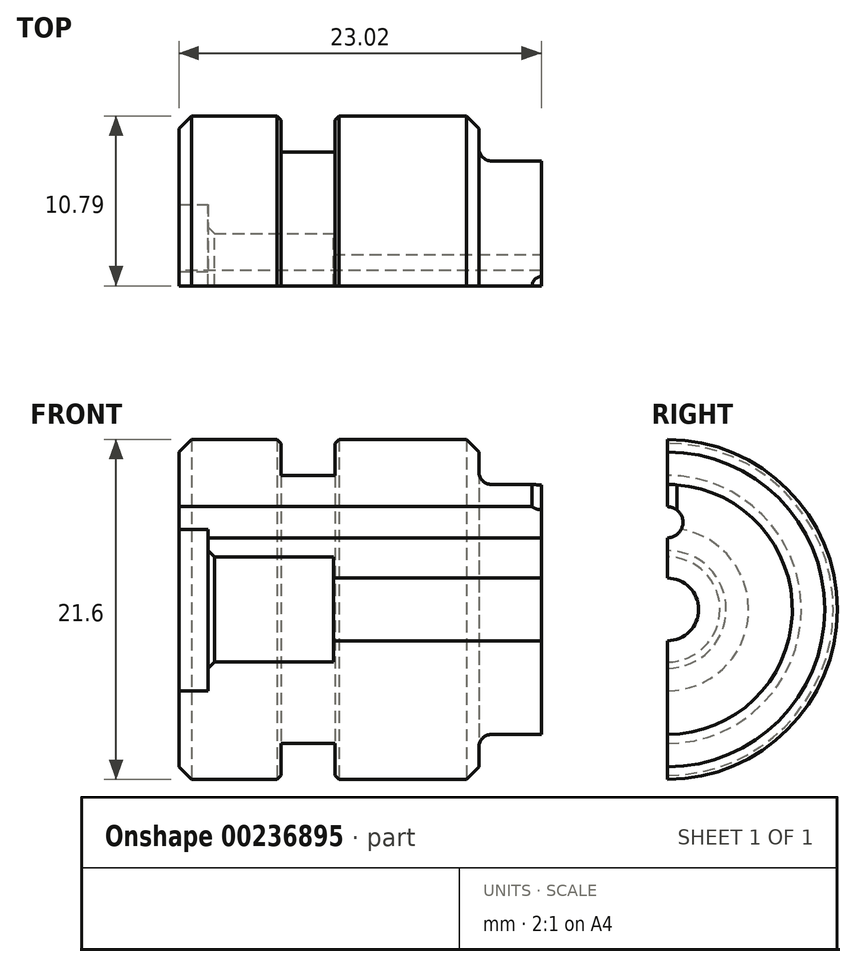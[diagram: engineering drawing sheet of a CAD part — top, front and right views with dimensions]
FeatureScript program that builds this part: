
annotation { "Feature Type Name" : "Feature", "Feature Type Description" : "" }
export const myFeature = defineFeature(function(context is Context, id is Id, definition is map)
    precondition{}
    {
        {
            var Q0;
            Q0=qCreatedBy(makeId("Front.planeOp"),FACE);
            var sketch = newSketch(context, id + "F0", { "sketchPlane" : qUnion([Q0])});
            skLineSegment(sketch, "E0.bottom", {"start": v(-29.86, 10.8) * mm, "end": v(-24.42, 10.8) * mm});
            skLineSegment(sketch, "E0.top", {"start": v(-30.66, 0) * mm, "end": v(0, 0) * mm});
            skLineSegment(sketch, "E0.left", {"start": v(-30.66, 10) * mm, "end": v(-30.66, 0) * mm});
            skLineSegment(sketch, "E0.right", {"start": v(0, 5.87) * mm, "end": v(0, 0) * mm});
            skLineSegment(sketch, "E1", {"start": v(-3.97, 7.94) * mm, "end": v(-10.81, 7.94) * mm});
            skLineSegment(sketch, "E2", {"start": v(-11.6, 8.73) * mm, "end": v(-11.6, 10) * mm});
            skLineSegment(sketch, "E3", {"start": v(-3.97, 7.94) * mm, "end": v(-1.57, 6.7) * mm});
            skPoint(sketch, "E4", {"position": v(-1.57, 6.7) * mm});
            skLineSegment(sketch, "E5", {"start": v(-1.57, 6.7) * mm, "end": v(0, 5.87) * mm});
            skPoint(sketch, "E6.visualSharp", {"position": v(-11.6, 7.94) * mm});
            skArc(sketch, "E6.filletArc", {"start": v(-11.6, 8.73) * mm, "mid": v(-11.38, 8.17) * mm, "end": v(-10.81, 7.94) * mm});
            skLineSegment(sketch, "E7", {"start": v(-12.4, 10.8) * mm, "end": v(-11.6, 10) * mm});
            skLineSegment(sketch, "E8", {"start": v(-30.66, 10) * mm, "end": v(-29.86, 10.8) * mm});
            skLineSegment(sketch, "E9.top", {"start": v(-24.16, 8.5) * mm, "end": v(-20.74, 8.5) * mm});
            skLineSegment(sketch, "E9.left", {"start": v(-24.16, 10.54) * mm, "end": v(-24.16, 8.5) * mm});
            skLineSegment(sketch, "E9.right", {"start": v(-20.74, 10.54) * mm, "end": v(-20.74, 8.5) * mm});
            skLineSegment(sketch, "E10.trimOffspring", {"start": v(-20.48, 10.8) * mm, "end": v(-12.4, 10.8) * mm});
            skLineSegment(sketch, "E11", {"start": v(-24.42, 10.8) * mm, "end": v(-24.16, 10.54) * mm});
            skLineSegment(sketch, "E12", {"start": v(-20.74, 10.54) * mm, "end": v(-20.48, 10.8) * mm});
            skSolve(sketch);
        }
        {
            var Q0;
            Q0=makeQuery(id+"F0.imprint","IMPRINT",FACE,{"disambiguationData":[TD([[makeQuery(id+"F0.imprint","IMPRINT",EDGE,{"derivedFrom":sQuery(id+"F0.wireOp",EDGE,"E0.bottom")}),-1.0]])]});
            var Q1;
            Q1=sQuery(id+"F0.wireOp",EDGE,"E0.top");
            revolve(context, id + "F1", {"entities" : qUnion([Q0]), "axis" : qUnion([Q1]), "revolveType" : RevolveType.FULL});
        }
        {
            var Q0;
            Q0=makeQuery(id+"F1.opRevolve","SWEPT_FACE",FACE,{"disambiguationData":[OSD([sQuery(id+"F0.wireOp",EDGE,"E0.right")])]});
            var sketch = newSketch(context, id + "F2", { "sketchPlane" : qUnion([Q0])});
            skCircle(sketch, "E13", {"center": v(0, 0) * mm, "radius": 1.98 * mm});
            skSolve(sketch);
        }
        {
            var Q0;
            Q0 = qSketchRegion(id + "F2", true);
            extrude(context, id + "F3", {"entities" : qUnion([Q0]), "operationType" : NewBodyOperationType.REMOVE, "endBound" : BoundingType.THROUGH_ALL, "oppositeDirection" : true, "depth" : 25.4 * mm});
        }
        {
            var Q0;
            Q0=qCreatedBy(makeId("Front.planeOp"),FACE);
            var sketch = newSketch(context, id + "F4", { "sketchPlane" : qUnion([Q0])});
            skLineSegment(sketch, "E14.bottom", {"start": v(-30.66, 0) * mm, "end": v(-28.8, 0) * mm});
            skLineSegment(sketch, "E14.top", {"start": v(-30.66, 5.16) * mm, "end": v(-28.8, 5.16) * mm});
            skLineSegment(sketch, "E14.left", {"start": v(-30.66, 0) * mm, "end": v(-30.66, 5.16) * mm});
            skLineSegment(sketch, "E14.right", {"start": v(-28.8, 3.74) * mm, "end": v(-28.8, 5.16) * mm});
            skLineSegment(sketch, "E15.bottom", {"start": v(-28.4, 3.34) * mm, "end": v(-20.85, 3.34) * mm});
            skLineSegment(sketch, "E15.top", {"start": v(-28.8, 0) * mm, "end": v(-20.85, 0) * mm});
            skLineSegment(sketch, "E15.right", {"start": v(-20.85, 3.34) * mm, "end": v(-20.85, 0) * mm});
            skLineSegment(sketch, "E16", {"start": v(-28.8, 3.74) * mm, "end": v(-28.4, 3.34) * mm});
            skSolve(sketch);
        }
        {
            var Q0;
            Q0 = qSketchRegion(id + "F4", true);
            var Q1;
            Q1=sQuery(id+"F4.wireOp",EDGE,"E15.top");
            revolve(context, id + "F5", {"operationType" : NewBodyOperationType.REMOVE, "entities" : qUnion([Q0]), "axis" : qUnion([Q1]), "revolveType" : RevolveType.FULL, "oppositeDirection" : true});
        }
        {
            var Q0;
            Q0=qCreatedBy(makeId("Front.planeOp"),FACE);
            var sketch = newSketch(context, id + "F6", { "sketchPlane" : qUnion([Q0])});
            skLineSegment(sketch, "E17.bottom", {"start": v(-30.66, 6.55) * mm, "end": v(-5.26, 6.55) * mm});
            skLineSegment(sketch, "E17.top", {"start": v(-30.66, 5.56) * mm, "end": v(-22.47, 5.56) * mm});
            skLineSegment(sketch, "E17.left", {"start": v(-30.66, 6.55) * mm, "end": v(-30.66, 5.56) * mm});
            skLineSegment(sketch, "E18", {"start": v(-5.26, 6.55) * mm, "end": v(-4.66, 5.56) * mm});
            skLineSegment(sketch, "E19", {"start": v(-4.66, 5.56) * mm, "end": v(-22.47, 5.56) * mm});
            skSolve(sketch);
        }
        {
            var Q0;
            Q0=qCreatedBy(makeId("Front.planeOp"),FACE);
            var sketch = newSketch(context, id + "F7", { "sketchPlane" : qUnion([Q0])});
            skLineSegment(sketch, "E20.bottom", {"start": v(-8.23, 5.56) * mm, "end": v(-7.64, 5.56) * mm});
            skLineSegment(sketch, "E20.top", {"start": v(-8.23, 10.2) * mm, "end": v(-7.64, 10.2) * mm});
            skLineSegment(sketch, "E20.left", {"start": v(-8.23, 10.2) * mm, "end": v(-8.23, 5.56) * mm});
            skPoint(sketch, "E21", {"position": v(-7.64, 5.56) * mm});
            skLineSegment(sketch, "E22", {"start": v(-7.64, 10.2) * mm, "end": v(-7.64, 5.56) * mm});
            skSolve(sketch);
        }
        {
            var Q0;
            Q0 = qSketchRegion(id + "F7", true);
            var Q1;
            Q1=sQuery(id+"F7.wireOp",EDGE,"E22");
            revolve(context, id + "F8", {"operationType" : NewBodyOperationType.REMOVE, "entities" : qUnion([Q0]), "axis" : qUnion([Q1]), "revolveType" : RevolveType.FULL, "oppositeDirection" : true});
        }
        {
            var Q0;
            Q0=makeQuery(id+"F1.opRevolve","SWEPT_FACE",FACE,{"disambiguationData":[OSD([sQuery(id+"F0.wireOp",EDGE,"E0.left")])]});
            var sketch = newSketch(context, id + "F9", { "sketchPlane" : qUnion([Q0])});
            skLineSegment(sketch, "E23", {"start": v(0, 0) * mm, "end": v(0, 14.89) * mm});
            skLineSegment(sketch, "E24", {"start": v(0, 14.89) * mm, "end": v(12.7, 14.89) * mm});
            skLineSegment(sketch, "E25", {"start": v(12.7, 14.89) * mm, "end": v(12.7, -15.47) * mm});
            skLineSegment(sketch, "E26", {"start": v(12.7, -15.47) * mm, "end": v(0, -15.47) * mm});
            skLineSegment(sketch, "E27", {"start": v(0, -15.47) * mm, "end": v(0, 0) * mm});
            skSolve(sketch);
        }
        {
            var Q0;
            Q0=makeQuery(id+"F1.opRevolve","SWEPT_FACE",FACE,{"disambiguationData":[OSD([sQuery(id+"F0.wireOp",EDGE,"E0.left")])]});
            var sketch = newSketch(context, id + "F10", { "sketchPlane" : qUnion([Q0])});
            skCircle(sketch, "E28", {"center": v(0, 5.54) * mm, "radius": 1 * mm});
            skLineSegment(sketch, "E29", {"start": v(0, 5.54) * mm, "end": v(0, 0) * mm, "construction": true});
            skSolve(sketch);
        }
        {
            var Q0;
            {var subQ0=sQuery(id+"F10.wireOp",EDGE,"E28");var subQ1=makeQuery(id+"F5.boolean.opBoolean","COPY",EDGE,{"derivedFrom":makeQuery(id+"F5.opRevolve","SWEPT_EDGE",EDGE,{"disambiguationData":[OSD([sQuery(id+"F4.wireOp",EDGE,"E14.top"),sQuery(id+"F4.wireOp",EDGE,"E14.left")])]})});var subQ2=makeQuery(id+"F10.imprint","INTERSECT",VERTEX,{"disambiguationData":[OD(0.0)],"derivedFrom":[subQ1,subQ0]});Q0=makeQuery(id+"F10.imprint","IMPRINT",FACE,{"disambiguationData":[TD([[makeQuery(id+"F10.imprint","IMPRINT",EDGE,{"disambiguationData":[TD([[subQ2,1.0]])],"derivedFrom":subQ0}),1.0]])]});}
            var Q1;
            {var subQ0=sQuery(id+"F10.wireOp",EDGE,"E28");var subQ1=makeQuery(id+"F5.boolean.opBoolean","COPY",EDGE,{"derivedFrom":makeQuery(id+"F5.opRevolve","SWEPT_EDGE",EDGE,{"disambiguationData":[OSD([sQuery(id+"F4.wireOp",EDGE,"E14.top"),sQuery(id+"F4.wireOp",EDGE,"E14.left")])]})});var subQ2=makeQuery(id+"F10.imprint","INTERSECT",VERTEX,{"disambiguationData":[OD(0.0)],"derivedFrom":[subQ1,subQ0]});Q1=makeQuery(id+"F10.imprint","IMPRINT",FACE,{"disambiguationData":[TD([[makeQuery(id+"F10.imprint","IMPRINT",EDGE,{"disambiguationData":[TD([[subQ2,-1.0]])],"derivedFrom":subQ0}),1.0]])]});}
            extrude(context, id + "F11", {"entities" : qUnion([Q0, Q1]), "operationType" : NewBodyOperationType.REMOVE, "oppositeDirection" : true, "depth" : 25.4 * mm});
        }
        {
            var Q0;
            Q0 = qSketchRegion(id + "F9", true);
            extrude(context, id + "F12", {"entities" : qUnion([Q0]), "operationType" : NewBodyOperationType.REMOVE, "endBound" : BoundingType.THROUGH_ALL, "oppositeDirection" : true, "depth" : 25.4 * mm});
        }
        {
            var Q0;
            Q0=makeQuery(id+"F1.opRevolve","SWEPT_EDGE",EDGE,{"disambiguationData":[OSD([sQuery(id+"F0.wireOp",EDGE,"E0.right"),sQuery(id+"F0.wireOp",EDGE,"E5")])]});
            fillet(context, id + "F13", {"entities" : qUnion([Q0]), "radius" : 0.25 * mm, "tangentPropagation" : true, "allowEdgeOverflow" : false});
        }
        {
            var Q0;
            Q0=makeQuery(id+"F12.boolean.opBoolean","COPY",FACE,{"disambiguationData":[TD([makeQuery(id+"F1.opRevolve","SWEPT_FACE",FACE,{"disambiguationData":[OSD([sQuery(id+"F0.wireOp",EDGE,"E0.bottom")])]}),makeQuery(id+"F1.opRevolve","SWEPT_FACE",FACE,{"disambiguationData":[OSD([sQuery(id+"F0.wireOp",EDGE,"E0.left")])]}),makeQuery(id+"F1.opRevolve","SWEPT_FACE",FACE,{"disambiguationData":[OSD([sQuery(id+"F0.wireOp",EDGE,"E1")])]}),makeQuery(id+"F1.opRevolve","SWEPT_FACE",FACE,{"disambiguationData":[OSD([sQuery(id+"F0.wireOp",EDGE,"E2")])]}),makeQuery(id+"F1.opRevolve","SWEPT_FACE",FACE,{"disambiguationData":[OSD([sQuery(id+"F0.wireOp",EDGE,"E6.filletArc")])]}),makeQuery(id+"F1.opRevolve","SWEPT_FACE",FACE,{"disambiguationData":[OSD([sQuery(id+"F0.wireOp",EDGE,"E7")])]}),makeQuery(id+"F1.opRevolve","SWEPT_FACE",FACE,{"disambiguationData":[OSD([sQuery(id+"F0.wireOp",EDGE,"E8")])]}),makeQuery(id+"F1.opRevolve","SWEPT_FACE",FACE,{"disambiguationData":[OSD([sQuery(id+"F0.wireOp",EDGE,"E9.top")])]}),makeQuery(id+"F1.opRevolve","SWEPT_FACE",FACE,{"disambiguationData":[OSD([sQuery(id+"F0.wireOp",EDGE,"E9.left")])]}),makeQuery(id+"F1.opRevolve","SWEPT_FACE",FACE,{"disambiguationData":[OSD([sQuery(id+"F0.wireOp",EDGE,"E9.right")])]}),makeQuery(id+"F1.opRevolve","SWEPT_FACE",FACE,{"disambiguationData":[OSD([sQuery(id+"F0.wireOp",EDGE,"E10.trimOffspring")])]}),makeQuery(id+"F1.opRevolve","SWEPT_FACE",FACE,{"disambiguationData":[OSD([sQuery(id+"F0.wireOp",EDGE,"E11")])]}),makeQuery(id+"F1.opRevolve","SWEPT_FACE",FACE,{"disambiguationData":[OSD([sQuery(id+"F0.wireOp",EDGE,"E12")])]}),makeQuery(id+"F8.boolean.opBoolean","COPY",FACE,{"derivedFrom":makeQuery(id+"F8.opRevolve","SWEPT_FACE",FACE,{"disambiguationData":[OSD([sQuery(id+"F7.wireOp",EDGE,"E20.left")])]})}),makeQuery(id+"F11.boolean.opBoolean","COPY",FACE,{"derivedFrom":makeQuery(id+"F11.opExtrude","SWEPT_FACE",FACE,{"disambiguationData":[OSD([sQuery(id+"F10.wireOp",EDGE,"E28")])]})})])],"derivedFrom":makeQuery(id+"F12.opExtrude","SWEPT_FACE",FACE,{"disambiguationData":[OSD([sQuery(id+"F9.wireOp",EDGE,"E23"),sQuery(id+"F9.wireOp",EDGE,"E27")])]})});
            var sketch = newSketch(context, id + "F14", { "sketchPlane" : qUnion([Q0])});
            skLineSegment(sketch, "E30", {"start": v(-7.64, 11.2) * mm, "end": v(-7.64, -10.42) * mm});
            skLineSegment(sketch, "E31", {"start": v(-8.23, 7.94) * mm, "end": v(-7.04, 7.94) * mm, "construction": true});
            skPoint(sketch, "E32", {"position": v(-7.64, 7.94) * mm});
            skLineSegment(sketch, "E33", {"start": v(-7.64, 11.2) * mm, "end": v(1.43, 11.2) * mm});
            skLineSegment(sketch, "E34", {"start": v(1.43, 11.2) * mm, "end": v(1.43, -10.4) * mm});
            skLineSegment(sketch, "E35", {"start": v(1.43, -10.4) * mm, "end": v(-7.64, -10.42) * mm});
            skSolve(sketch);
        }
        {
            var Q0;
            Q0=makeQuery(id+"F14.imprint","IMPRINT",FACE,{"disambiguationData":[TD([[makeQuery(id+"F14.imprint","IMPRINT",EDGE,{"derivedFrom":sQuery(id+"F14.wireOp",EDGE,"E30")}),1.0]])]});
            extrude(context, id + "F15", {"entities" : qUnion([Q0]), "operationType" : NewBodyOperationType.REMOVE, "oppositeDirection" : true, "depth" : 25.4 * mm});
        }
    });
